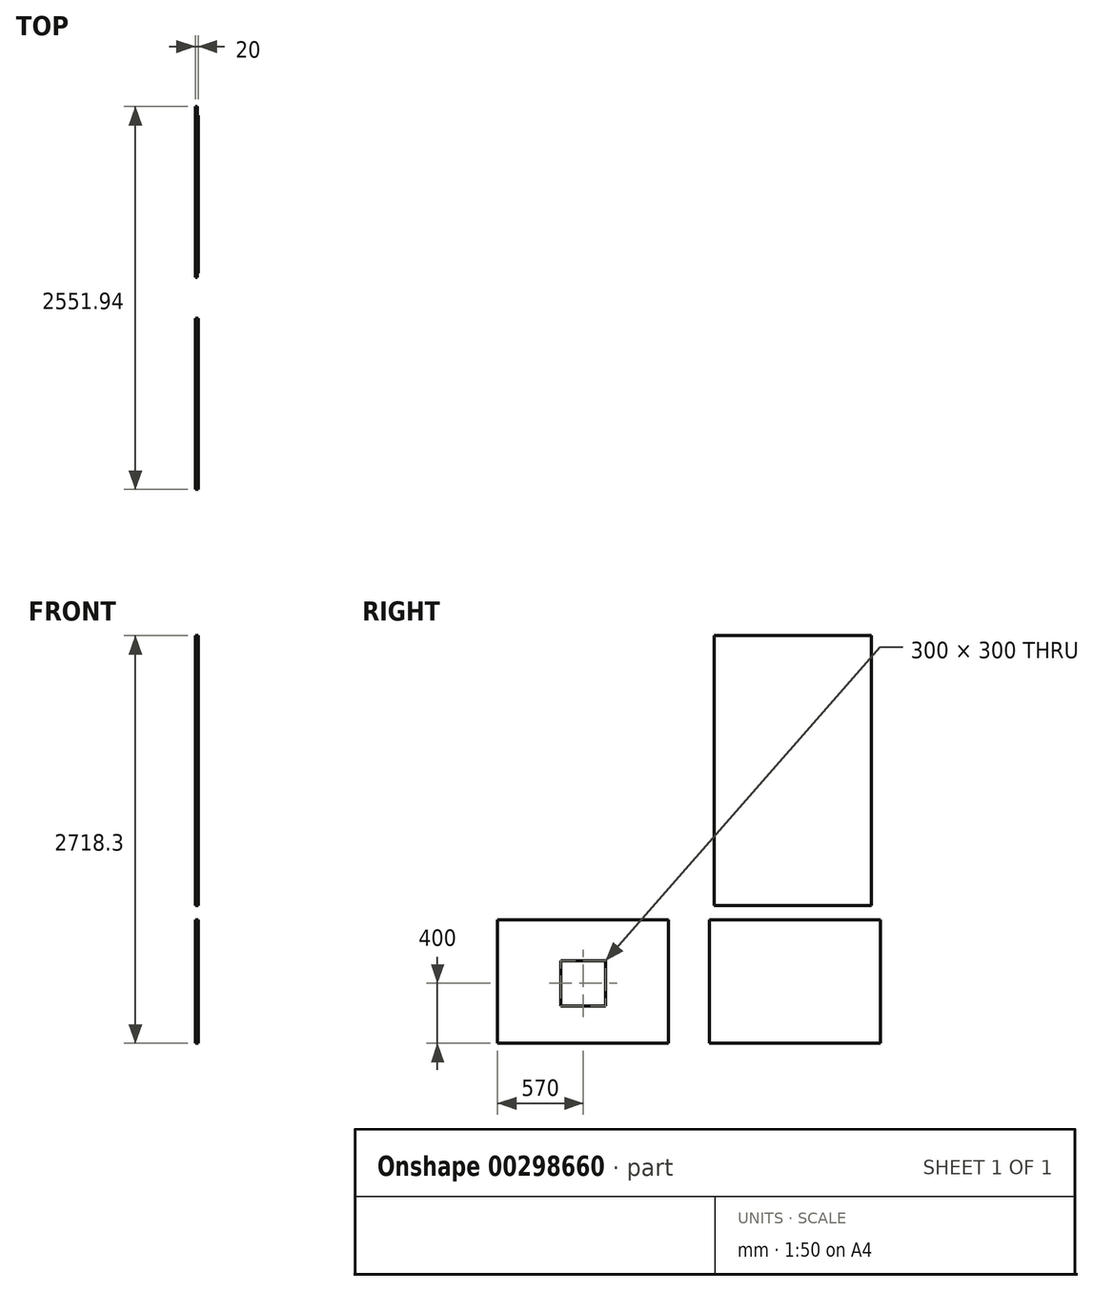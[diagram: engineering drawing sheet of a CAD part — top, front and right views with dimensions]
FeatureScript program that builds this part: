
annotation { "Feature Type Name" : "Feature", "Feature Type Description" : "" }
export const myFeature = defineFeature(function(context is Context, id is Id, definition is map)
    precondition{}
    {
        {
            var Q0;
            Q0=qCreatedBy(makeId("Right.planeOp"),FACE);
            var sketch = newSketch(context, id + "F0", { "sketchPlane" : qUnion([Q0])});
            skLineSegment(sketch, "E0.bottom", {"start": v(0, 0) * mm, "end": v(1140, 0) * mm});
            skLineSegment(sketch, "E0.top", {"start": v(0, 825) * mm, "end": v(1140, 825) * mm});
            skLineSegment(sketch, "E0.left", {"start": v(0, 0) * mm, "end": v(0, 825) * mm});
            skLineSegment(sketch, "E0.right", {"start": v(1140, 0) * mm, "end": v(1140, 825) * mm});
            skLineSegment(sketch, "E1", {"start": v(570, 825) * mm, "end": v(570, 0) * mm, "construction": true});
            skLineSegment(sketch, "E2.bottom", {"start": v(720, 250) * mm, "end": v(420, 250) * mm});
            skLineSegment(sketch, "E2.top", {"start": v(720, 550) * mm, "end": v(420, 550) * mm});
            skLineSegment(sketch, "E2.left", {"start": v(720, 250) * mm, "end": v(720, 550) * mm});
            skLineSegment(sketch, "E2.right", {"start": v(420, 250) * mm, "end": v(420, 550) * mm});
            skPoint(sketch, "E2.middle", {"position": v(570, 400) * mm});
            skSolve(sketch);
        }
        {
            var Q0;
            Q0=makeQuery(id+"F0.imprint","IMPRINT",FACE,{"disambiguationData":[TD([[makeQuery(id+"F0.imprint","IMPRINT",EDGE,{"derivedFrom":sQuery(id+"F0.wireOp",EDGE,"E0.bottom")}),1.0]])]});
            extrude(context, id + "F1", {"entities" : qUnion([Q0]), "depth" : 20 * mm});
        }
        {
            var Q0;
            Q0=qCreatedBy(makeId("Right.planeOp"),FACE);
            var sketch = newSketch(context, id + "F2", { "sketchPlane" : qUnion([Q0])});
            skLineSegment(sketch, "E3.bottom", {"start": v(1411.94, 0) * mm, "end": v(2551.94, 0) * mm});
            skLineSegment(sketch, "E3.top", {"start": v(1411.94, 825) * mm, "end": v(2551.94, 825) * mm});
            skLineSegment(sketch, "E3.left", {"start": v(1411.94, 0) * mm, "end": v(1411.94, 825) * mm});
            skLineSegment(sketch, "E3.right", {"start": v(2551.94, 0) * mm, "end": v(2551.94, 825) * mm});
            skSolve(sketch);
        }
        {
            var Q0;
            Q0 = qSketchRegion(id + "F2", true);
            extrude(context, id + "F3", {"entities" : qUnion([Q0]), "depth" : 15 * mm});
        }
        {
            var Q0;
            Q0=qCreatedBy(makeId("Right.planeOp"),FACE);
            var sketch = newSketch(context, id + "F4", { "sketchPlane" : qUnion([Q0])});
            skLineSegment(sketch, "E4.bottom", {"start": v(1441.67, 918.3) * mm, "end": v(2491.67, 918.3) * mm});
            skLineSegment(sketch, "E4.top", {"start": v(1441.67, 2718.3) * mm, "end": v(2491.67, 2718.3) * mm});
            skLineSegment(sketch, "E4.left", {"start": v(1441.67, 918.3) * mm, "end": v(1441.67, 2718.3) * mm});
            skLineSegment(sketch, "E4.right", {"start": v(2491.67, 918.3) * mm, "end": v(2491.67, 2718.3) * mm});
            skLineSegment(sketch, "E5", {"start": v(1966.67, 918.3) * mm, "end": v(1966.67, 2718.3) * mm, "construction": true});
            skSolve(sketch);
        }
        {
            var Q0;
            Q0 = qSketchRegion(id + "F4", true);
            extrude(context, id + "F5", {"entities" : qUnion([Q0]), "depth" : 20 * mm});
        }
    });
